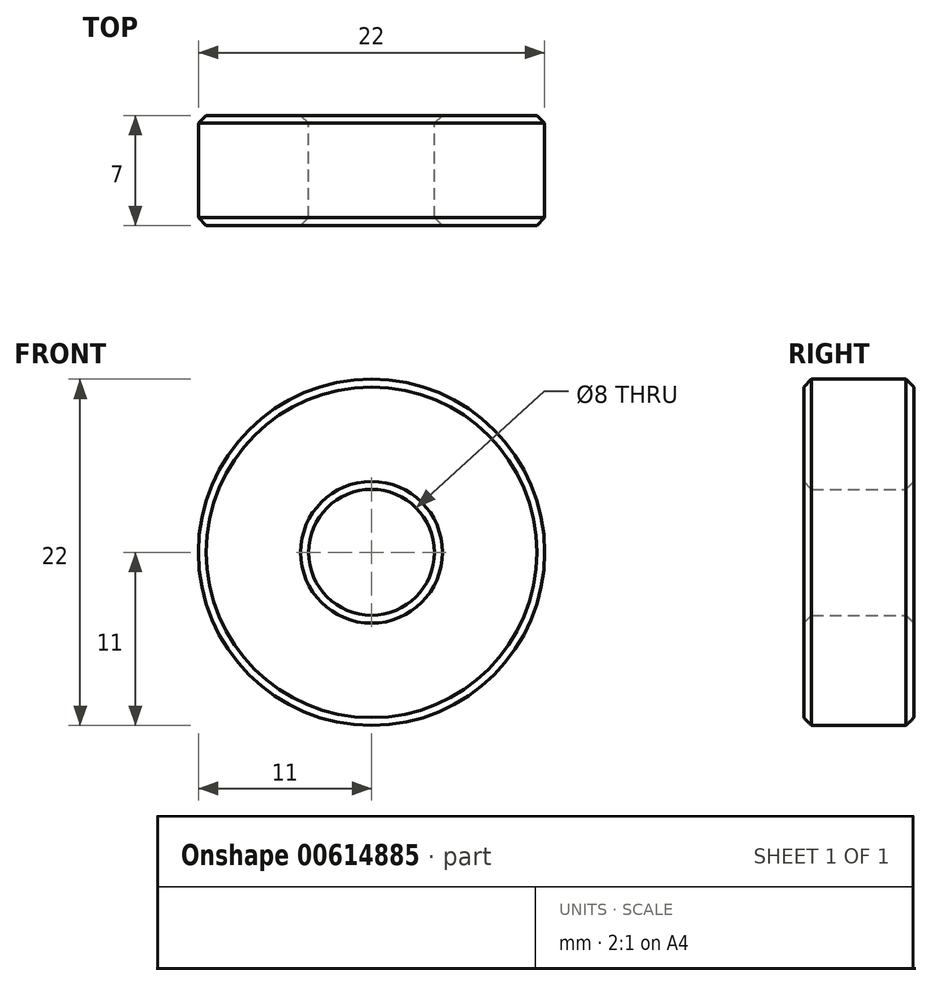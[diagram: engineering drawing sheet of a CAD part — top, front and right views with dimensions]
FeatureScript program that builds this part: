
annotation { "Feature Type Name" : "Feature", "Feature Type Description" : "" }
export const myFeature = defineFeature(function(context is Context, id is Id, definition is map)
    precondition{}
    {
        {
            var Q0;
            Q0=qCreatedBy(makeId("Front.planeOp"),FACE);
            var sketch = newSketch(context, id + "F0", { "sketchPlane" : qUnion([Q0])});
            skCircle(sketch, "E0", {"center": v(0, 0) * mm, "radius": 11 * mm});
            skCircle(sketch, "E1", {"center": v(0, 0) * mm, "radius": 4 * mm});
            skSolve(sketch);
        }
        {
            var Q0;
            Q0 = qSketchRegion(id + "F0", true);
            extrude(context, id + "F1", {"entities" : qUnion([Q0]), "depth" : 7 * mm, "offsetDistance" : 25 * mm});
        }
        {
            var Q0;
            Q0=makeQuery(id+"F1.opExtrude","SWEPT_FACE",FACE,{"disambiguationData":[OSD([sQuery(id+"F0.wireOp",EDGE,"E0")])]});
            var Q1;
            Q1=makeQuery(id+"F1.opExtrude","SWEPT_FACE",FACE,{"disambiguationData":[OSD([sQuery(id+"F0.wireOp",EDGE,"E1")])]});
            chamfer(context, id + "F2", {"entities" : qUnion([Q0, Q1]), "width" : 0.5 * mm, "tangentPropagation" : true});
        }
    });
